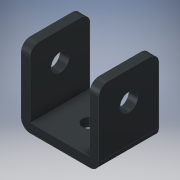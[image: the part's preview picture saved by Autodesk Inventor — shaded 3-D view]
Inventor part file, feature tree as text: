
AUTODESK INVENTOR PART (.ipt)
format: ipt  version: 2019.4 (Build 234330000, 330)  size: 148,480 bytes
history: native  units: mm
features: extrude x3, sketch x3, fillet x2
ambient origin geometry x8: Origin, YZ Plane, XZ Plane, XY Plane, X Axis, Y Axis, Z Axis, Center Point
bodies: Solid1 (feature_tree)
feature tree (8):
  extrude  "Extrusion1"  Depth=25.0mm
  extrude  "Extrusion2"  Depth=3.0mm
  extrude  "Extrusion3"  Depth=20.0mm TaperAngle=0.0deg
  fillet  "Fillet2"  Radius=20.0mm
  fillet  "Fillet3"  Radius=39.0mm
  sketch  "Sketch1"  dims[d0=26.0mm d1=25.0mm]
  sketch  "Sketch2"  dims[d2=3.0mm d3=3.0mm]
  sketch  "Sketch3"  dims[d4=3.0mm d5=20.0mm d6=0.0mm d7=20.0mm d9=39.0mm d10=0.0mm d11=5.0mm d12=39.0mm d13=0.0mm d15=3.0mm d16=3.0mm d17=6.0mm d20=3.0mm d21=12.5mm]
